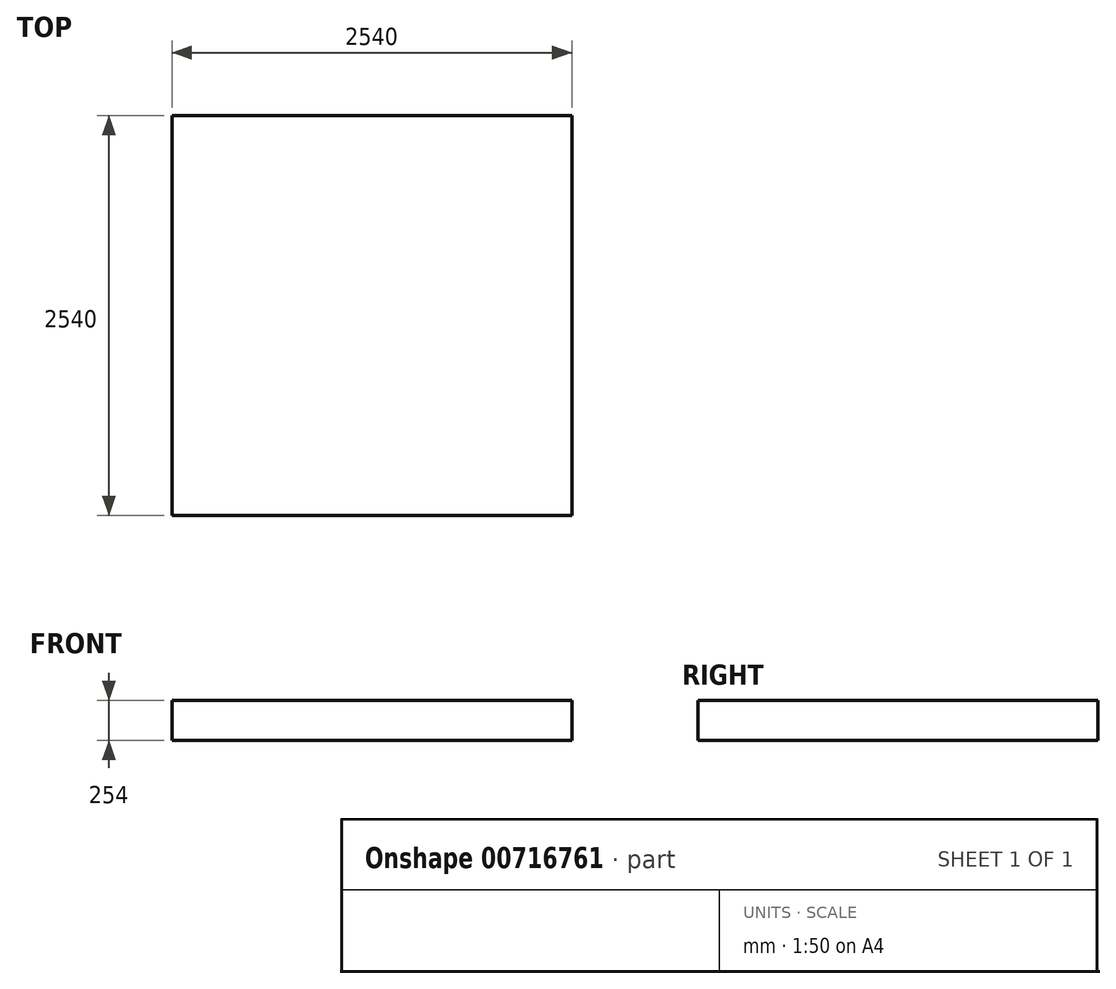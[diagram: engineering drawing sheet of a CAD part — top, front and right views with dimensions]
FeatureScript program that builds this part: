
annotation { "Feature Type Name" : "Feature", "Feature Type Description" : "" }
export const myFeature = defineFeature(function(context is Context, id is Id, definition is map)
    precondition{}
    {
        {
            var Q0;
            Q0=qCreatedBy(makeId("Top.planeOp"),FACE);
            var sketch = newSketch(context, id + "F0", { "sketchPlane" : qUnion([Q0])});
            skLineSegment(sketch, "E0.bottom", {"start": v(-1270, 1270) * mm, "end": v(1270, 1270) * mm});
            skLineSegment(sketch, "E0.top", {"start": v(-1270, -1270) * mm, "end": v(1270, -1270) * mm});
            skLineSegment(sketch, "E0.left", {"start": v(-1270, 1270) * mm, "end": v(-1270, -1270) * mm});
            skLineSegment(sketch, "E0.right", {"start": v(1270, 1270) * mm, "end": v(1270, -1270) * mm});
            skSolve(sketch);
        }
        {
            var Q0;
            Q0 = qSketchRegion(id + "F0", true);
            extrude(context, id + "F1", {"entities" : qUnion([Q0]), "depth" : 254 * mm, "offsetDistance" : 25.4 * mm});
        }
    });
